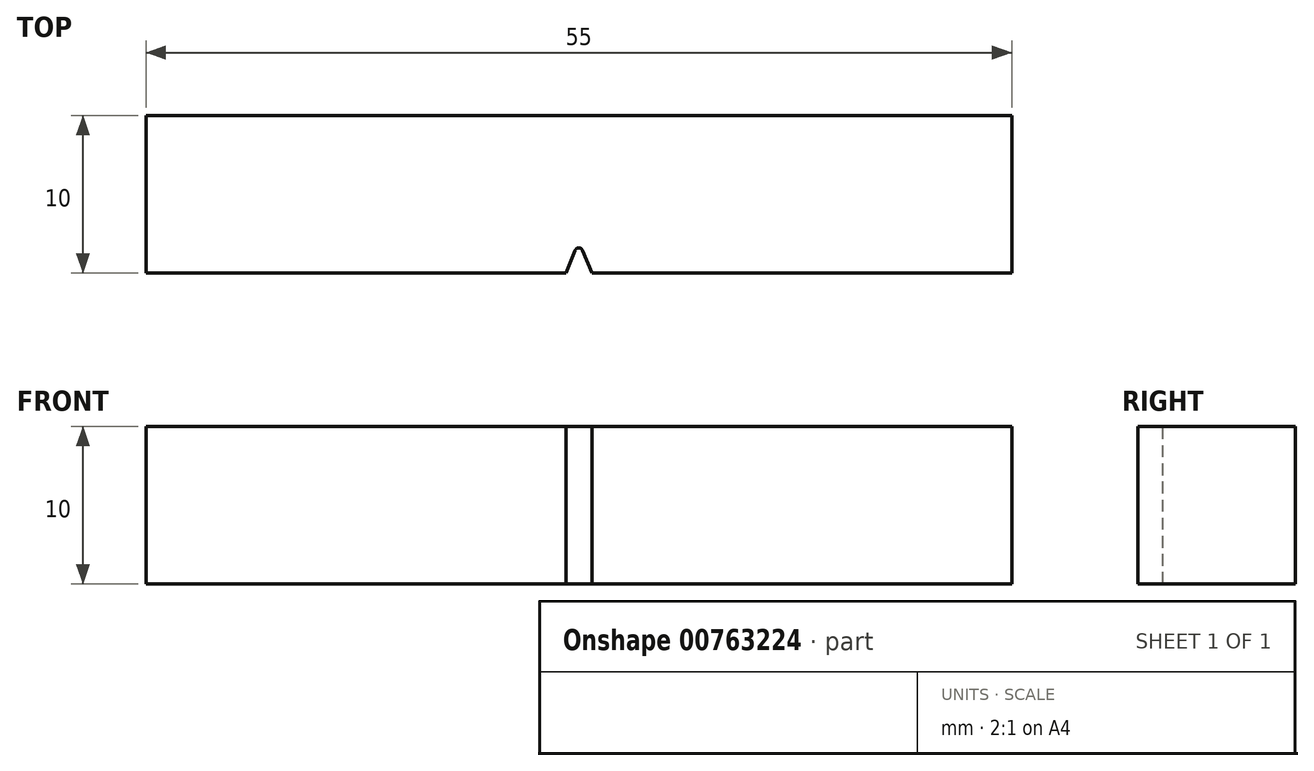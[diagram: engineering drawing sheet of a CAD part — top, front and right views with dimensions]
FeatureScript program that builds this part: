
annotation { "Feature Type Name" : "Feature", "Feature Type Description" : "" }
export const myFeature = defineFeature(function(context is Context, id is Id, definition is map)
    precondition{}
    {
        {
            var Q0;
            Q0=qCreatedBy(makeId("Top.planeOp"),FACE);
            var sketch = newSketch(context, id + "F0", { "sketchPlane" : qUnion([Q0])});
            skLineSegment(sketch, "E0.bottom", {"start": v(-27.5, 5) * mm, "end": v(27.5, 5) * mm});
            skLineSegment(sketch, "E0.top", {"start": v(-27.5, -5) * mm, "end": v(27.5, -5) * mm});
            skLineSegment(sketch, "E0.left", {"start": v(-27.5, 5) * mm, "end": v(-27.5, -5) * mm});
            skLineSegment(sketch, "E0.right", {"start": v(27.5, 5) * mm, "end": v(27.5, -5) * mm});
            skPoint(sketch, "E0.middle", {"position": v(0, 0) * mm});
            skLineSegment(sketch, "E1", {"start": v(-0.83, -5) * mm, "end": v(0, -3) * mm});
            skLineSegment(sketch, "E2", {"start": v(0, -3) * mm, "end": v(0.83, -5) * mm});
            skSolve(sketch);
        }
        {
            var Q0;
            Q0=makeQuery(id+"F0.imprint","IMPRINT",FACE,{"disambiguationData":[TD([[makeQuery(id+"F0.imprint","IMPRINT",EDGE,{"derivedFrom":sQuery(id+"F0.wireOp",EDGE,"E0.bottom")}),-1.0]])]});
            extrude(context, id + "F1", {"entities" : qUnion([Q0]), "depth" : 10 * mm, "offsetDistance" : 25 * mm});
        }
        {
            var Q0;
            Q0=makeQuery(id+"F1.opExtrude","SWEPT_EDGE",EDGE,{"disambiguationData":[OSD([sQuery(id+"F0.wireOp",EDGE,"E1"),sQuery(id+"F0.wireOp",EDGE,"E2")])]});
            fillet(context, id + "F2", {"entities" : qUnion([Q0]), "radius" : 0.25 * mm, "tangentPropagation" : true, "allowEdgeOverflow" : false});
        }
    });
